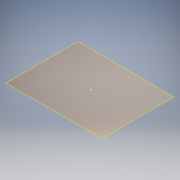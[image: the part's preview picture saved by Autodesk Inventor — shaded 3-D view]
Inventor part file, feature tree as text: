
AUTODESK INVENTOR PART (.ipt)
format: ipt  version: 2017 SP1 (Build 210196100, 196)  size: 83,456 bytes
history: native  units: mm
features: plane x1, sketch x1
ambient origin geometry x8: Origin, YZ Plane, XZ Plane, XY Plane, X Axis, Y Axis, Z Axis, Center Point
feature tree (2):
  plane  "Arbeitsebene1"
  sketch  "Skizze5"
